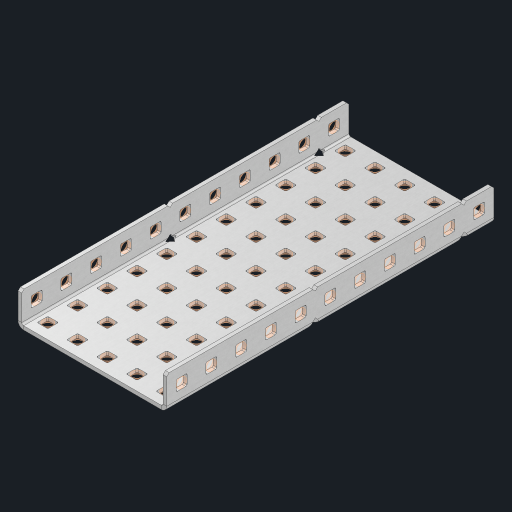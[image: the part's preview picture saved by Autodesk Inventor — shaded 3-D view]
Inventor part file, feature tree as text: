
AUTODESK INVENTOR PART (.ipt)
format: ipt  version: 2023 (Build 270158000, 158)  size: 1,104,384 bytes
history: native  units: in
note: dims shown in document units (in); Inventor stores cm internally (conversion verified against a paired STEP export)
features: other x82, extrude x76, sheet_metal_op x10, sketch x8, mirror x1, pattern_linear x1, chamfer x1
ambient origin geometry x8: Origin, YZ Plane, XZ Plane, XY Plane, X Axis, Y Axis, Z Axis, Center Point
bodies: Solid1 (feature_tree), Body (feature_tree)
feature tree (179):
  other  "Flange Pattern Plane"
  sheet_metal_op  "Flange Pattern"
  sheet_metal_op  "Body Pattern"
  other  "Arc Length"
  mirror  "Notch Mirror"
  pattern_linear  "Notch Pattern"  Spacing1=0.25in  [1 undecoded]
  chamfer  "End Chamfer"
  extrude  "Half Cut"  Depth=0.0625in
  sketch  "Sketch1"  dims[d0=2.5in]
  other  "Plate1"
  sketch  "Sketch2"  dims[d1=5.5in]
  other  "Plate2"
  sheet_metal_op  "Bend1"
  sheet_metal_op  "Corner1"
  sketch  "Sketch3"  dims[d2=0.0625in]
  other  "Flange Pattern Sketch"
  sketch  "Sketch7"  dims[d3=0.0625in]
  other  "Srf1"
  other  "Srf2"
  sketch  "Sketch8"  dims[d4=0.0312in]
  sketch  "Sketch9"  dims[d5=0.125in]
  other  "Srf91"
  sheet_metal_op  "Body Pattern Sketch"
  other  "Srf92"
  sketch  "Sketch13"  dims[d6=0.0625in]
  sketch  "Sketch14"  dims[d7=0.5in d8=90.0deg d9=0.0312in d10=0.25in d11=0.0625in d12=0.0625in d16=0.182in d17=0.02in d18=0.0625in d19=0.0in d20=0.25in d21=0.25in d46=0.172in d47=1.0in d48=0.0in d49=0.182in d50=0.02in d51=0.25in d52=0.25in d53=0.0625in d54=0.0in d55=0.172in d56=1.0in d57=0.0in d60=4.3307in d62=0.5in d63=1.9685in d65=0.5in d85=0.1473in d86=0.1782in d88=0.04in d89=0.0625in d90=0.0in d91=0.04in d92=0.0491in d95=2.5in d96=0.04in d97=0.25in d98=45.0deg d101=0.0in d102=2.497in d131=2.5in d132=4.3307in d134=0.5in d139=0.5in]
  other  "Srf856"
  other  "Srf1310"
  other  "Srf1311"
  other  "Srf1312"
  other  "Srf1376"
  other  "Srf1377"
  other  "Srf1728"
  other  "Srf1755"
  other  "Srf1878"
  other  "Srf1879"
  other  "Srf1880"
  other  "Srf1881"
  other  "Srf1882"
  other  "Srf1883"
  other  "Srf1884"
  other  "Srf1885"
  other  "Srf1886"
  other  "Srf1887"
  other  "Srf1888"
  other  "Srf1889"
  other  "Srf1890"
  other  "Srf1891"
  other  "Srf1892"
  other  "Srf1893"
  other  "Srf1942"
  other  "Srf1943"
  other  "Srf1944"
  other  "Srf1945"
  other  "Srf1946"
  other  "Srf1947"
  other  "Srf1948"
  other  "Srf1949"
  other  "Srf1950"
  other  "Srf1951"
  other  "Srf1952"
  other  "Srf1953"
  other  "Srf1954"
  other  "Srf1955"
  other  "Srf1956"
  other  "Srf1957"
  other  "Srf1958"
  other  "Srf1959"
  other  "Srf1960"
  other  "Srf1961"
  other  "Srf1962"
  other  "Srf1963"
  other  "Srf1964"
  other  "Srf1965"
  other  "Srf1966"
  other  "Srf1967"
  other  "Srf1968"
  other  "Srf1969"
  other  "Srf1970"
  other  "Srf2146"
  other  "Srf2147"
  other  "Srf2148"
  other  "Srf2149"
  other  "Srf2150"
  other  "Srf2151"
  other  "Srf2152"
  other  "Srf2153"
  other  "Srf2154"
  other  "Srf2155"
  other  "Srf2156"
  other  "Srf2157"
  other  "Srf2158"
  other  "Srf2159"
  other  "Srf2160"
  other  "Srf2161"
  other  "Srf2162"
  other  "Srf2163"
  other  "Srf2164"
  other  "Srf2165"
  sheet_metal_op  "Flange Stamp"
  sheet_metal_op  "Flange Circle"
  sheet_metal_op  "Body Stamp"
  sheet_metal_op  "Body Circle"
  sheet_metal_op  "Notch"
  extrude  "ExtrusionSrf2"  Depth=0.0625in
  extrude  "ExtrusionSrf92"  Depth=2.5in
  extrude  "ExtrusionSrf856"  Depth=0.02in
  extrude  "ExtrusionSrf1310"  Depth=0.0625in
  extrude  "ExtrusionSrf1311"  TaperAngle=0.0deg  [1 undecoded]
  extrude  "ExtrusionSrf1312"  Depth=0.25in
  extrude  "ExtrusionSrf1376"  Depth=0.25in
  extrude  "ExtrusionSrf1377"  Depth=2.5in
  extrude  "ExtrusionSrf1728"  Depth=2.5in TaperAngle=0.0deg
  extrude  "ExtrusionSrf1755"  Depth=2.5in
  extrude  "ExtrusionSrf1878"  Depth=0.02in
  extrude  "ExtrusionSrf1879"  Depth=0.25in
  extrude  "ExtrusionSrf1880"  Depth=0.25in
  extrude  "ExtrusionSrf1881"  Depth=0.0625in
  extrude  "ExtrusionSrf1882"  TaperAngle=0.0deg  [1 undecoded]
  extrude  "ExtrusionSrf1883"  Depth=2.5in
  extrude  "ExtrusionSrf1884"  Depth=2.5in TaperAngle=0.0deg
  extrude  "ExtrusionSrf1885"  Depth=2.5in
  extrude  "ExtrusionSrf1886"  Depth=2.5in
  extrude  "ExtrusionSrf1887"  Depth=2.5in
  extrude  "ExtrusionSrf1888"  Depth=2.5in
  extrude  "ExtrusionSrf1889"  Depth=2.5in
  extrude  "ExtrusionSrf1890"  Depth=0.0625in
  extrude  "ExtrusionSrf1891"  TaperAngle=0.0deg  [1 undecoded]
  extrude  "ExtrusionSrf1892"  Depth=2.5in
  extrude  "ExtrusionSrf1893"  Depth=2.5in
  extrude  "ExtrusionSrf1942"  Depth=2.5in
  extrude  "ExtrusionSrf1943"  Depth=0.25in TaperAngle=45.0deg
  extrude  "ExtrusionSrf1944"  TaperAngle=0.0deg  [1 undecoded]
  extrude  "ExtrusionSrf1945"  Depth=2.5in
  extrude  "ExtrusionSrf1946"  Depth=2.5in
  extrude  "ExtrusionSrf1947"  Depth=2.5in
  extrude  "ExtrusionSrf1948"  Depth=2.5in
  extrude  "ExtrusionSrf1949"  Depth=2.5in
  extrude  "ExtrusionSrf1950"  [1 undecoded]
  extrude  "ExtrusionSrf1951"  [1 undecoded]
  extrude  "ExtrusionSrf1952"  [1 undecoded]
  extrude  "ExtrusionSrf1953"  [1 undecoded]
  extrude  "ExtrusionSrf1954"  [1 undecoded]
  extrude  "ExtrusionSrf1955"  [1 undecoded]
  extrude  "ExtrusionSrf1956"  [1 undecoded]
  extrude  "ExtrusionSrf1957"  [1 undecoded]
  extrude  "ExtrusionSrf1958"  [1 undecoded]
  extrude  "ExtrusionSrf1959"  [1 undecoded]
  extrude  "ExtrusionSrf1960"  [1 undecoded]
  extrude  "ExtrusionSrf1961"  [1 undecoded]
  extrude  "ExtrusionSrf1962"  [1 undecoded]
  extrude  "ExtrusionSrf1963"  [1 undecoded]
  extrude  "ExtrusionSrf1964"  [1 undecoded]
  extrude  "ExtrusionSrf1965"  [1 undecoded]
  extrude  "ExtrusionSrf1966"  [1 undecoded]
  extrude  "ExtrusionSrf1967"  [1 undecoded]
  extrude  "ExtrusionSrf1968"  [1 undecoded]
  extrude  "ExtrusionSrf1969"  [1 undecoded]
  extrude  "ExtrusionSrf1970"  [1 undecoded]
  extrude  "ExtrusionSrf2146"  [1 undecoded]
  extrude  "ExtrusionSrf2147"  [1 undecoded]
  extrude  "ExtrusionSrf2148"  [1 undecoded]
  extrude  "ExtrusionSrf2149"  [1 undecoded]
  extrude  "ExtrusionSrf2150"  [1 undecoded]
  extrude  "ExtrusionSrf2151"  [1 undecoded]
  extrude  "ExtrusionSrf2152"  [1 undecoded]
  extrude  "ExtrusionSrf2153"  [1 undecoded]
  extrude  "ExtrusionSrf2154"  [1 undecoded]
  extrude  "ExtrusionSrf2155"  [1 undecoded]
  extrude  "ExtrusionSrf2156"  [1 undecoded]
  extrude  "ExtrusionSrf2157"  [1 undecoded]
  extrude  "ExtrusionSrf2158"  [1 undecoded]
  extrude  "ExtrusionSrf2159"  [1 undecoded]
  extrude  "ExtrusionSrf2160"  [1 undecoded]
  extrude  "ExtrusionSrf2161"  [1 undecoded]
  extrude  "ExtrusionSrf2162"  [1 undecoded]
  extrude  "ExtrusionSrf2163"  [1 undecoded]
  extrude  "ExtrusionSrf2164"  [1 undecoded]
  extrude  "ExtrusionSrf2165"  [1 undecoded]
note: 46 required parameter values undecoded (feature->parameter linkage not recoverable at this tier; creation-order binding heuristic only, values carry confidence <= 0.55)
